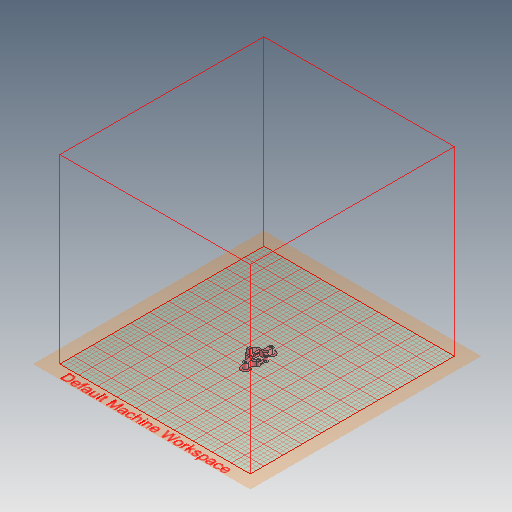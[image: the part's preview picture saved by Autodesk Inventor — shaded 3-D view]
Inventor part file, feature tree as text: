
AUTODESK INVENTOR PART (.ipt)
format: ipt  version: 2021 (Build 250183000, 183)  size: 694,272 bytes
history: native  units: mm
features: sketch x10, extrude x8, other x3, loft x1, mirror x1
ambient origin geometry x8: Origin, YZ Plane, XZ Plane, XY Plane, X Axis, Y Axis, Z Axis, Center Point
bodies: Body1 (feature_tree)
feature tree (23):
  other  "Sólido1"
  extrude  "Extrusão1"  Depth=8.0mm
  extrude  "Extrusão2"  Depth=17.0mm
  extrude  "Extrusão3"  Depth=28.0mm
  extrude  "Extrusão4"  Depth=10.0mm
  extrude  "Extrusão7"  Depth=10.0mm
  extrude  "Extrusão10"  Depth=12.0mm
  sketch  "Esboço13"  dims[d25=20.0mm d26=3.0mm d27=0.0mm]
  other  "Plano de trabalho1"
  loft  "Transição1"
  mirror  "Espelhamento1"
  extrude  "Extrusão11"  Depth=12.0mm
  extrude  "Extrusão12"  Depth=3.0mm TaperAngle=0.0deg
  sketch  "Esboço1"  dims[d0=5.0mm d1=8.0mm]
  sketch  "Esboço2"  dims[d2=20.0mm d3=17.0mm]
  sketch  "Esboço3"  dims[d4=20.0mm d6=28.0mm]
  sketch  "Esboço4"  dims[d7=2.0mm d10=10.0mm]
  sketch  "Esboço7"  dims[d11=10.0mm d13=2.0mm]
  other  "Contorno projetado1"
  sketch  "Esboço10"  dims[d14=12.0mm d15=0.0mm d16=5.5mm]
  sketch  "Esboço11"  dims[d18=3.0mm d19=2.0mm]
  sketch  "Esboço12"  dims[d22=3.5mm d23=0.0mm d24=12.0mm]
  sketch  "Esboço14"  dims[d30=10.0mm d31=10.5mm d32=0.0mm d46=6.0mm d47=0.0mm d48=0.0mm d57=16.5mm d58=3.5mm d59=22.0mm d60=21.0mm d61=0.0mm d62=1.5mm d63=19.3mm d67=6.0mm d68=0.0mm d69=5.0mm d70=5.0mm d71=0.2mm d72=0.0mm d73=2.5mm d77=-5.0mm d78=0.0mm d79=90.0deg d80=0.0mm d81=90.0deg d41=0.5mm d42=0.872665mm d43=0.5mm d44=0.872665mm d64=0.5mm d65=0.872665mm]
